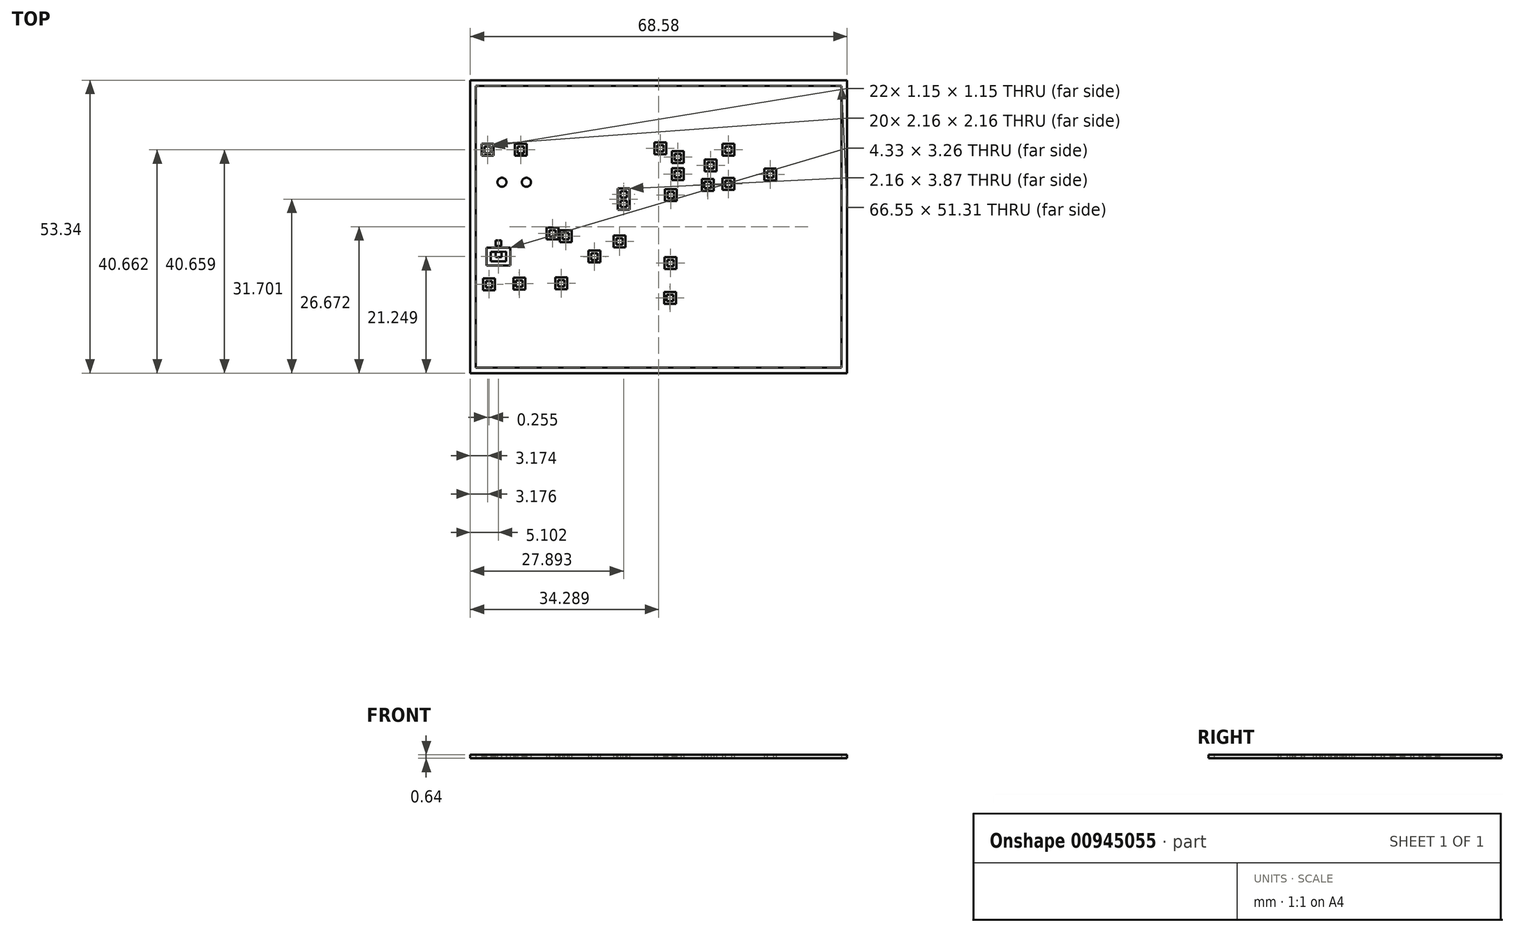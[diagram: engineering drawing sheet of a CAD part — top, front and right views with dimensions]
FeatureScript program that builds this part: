
annotation { "Feature Type Name" : "Feature", "Feature Type Description" : "" }
export const myFeature = defineFeature(function(context is Context, id is Id, definition is map)
    precondition{}
    {
        {
            var Q0;
            Q0=qCreatedBy(makeId("Top.planeOp"),FACE);
            var sketch = newSketch(context, id + "F0", { "sketchPlane" : qUnion([Q0])});
            skLineSegment(sketch, "E0.bottom", {"start": v(-43.28, 27.91) * mm, "end": v(25.3, 27.91) * mm});
            skLineSegment(sketch, "E0.top", {"start": v(-43.28, -25.43) * mm, "end": v(25.3, -25.43) * mm});
            skLineSegment(sketch, "E0.left", {"start": v(-43.28, 27.91) * mm, "end": v(-43.28, -25.43) * mm});
            skCircle(sketch, "E1", {"center": v(-37.53, 9.34) * mm, "radius": 0.82 * mm});
            skCircle(sketch, "E2", {"center": v(-37.53, 9.34) * mm, "radius": 1.33 * mm});
            skCircle(sketch, "E3", {"center": v(-33.07, 9.34) * mm, "radius": 0.83 * mm});
            skCircle(sketch, "E4", {"center": v(-33.07, 9.34) * mm, "radius": 1.33 * mm});
            skLineSegment(sketch, "E5.top", {"start": v(-39.58, -5.05) * mm, "end": v(-36.77, -5.05) * mm});
            skLineSegment(sketch, "E5.left", {"start": v(-39.58, -3.31) * mm, "end": v(-39.58, -5.05) * mm});
            skLineSegment(sketch, "E5.right", {"start": v(-36.77, -3.3) * mm, "end": v(-36.77, -5.05) * mm});
            skLineSegment(sketch, "E6.bottom", {"start": v(-38.67, -3.31) * mm, "end": v(-37.61, -3.31) * mm});
            skLineSegment(sketch, "E6.top", {"start": v(-38.67, -4.3) * mm, "end": v(-37.61, -4.3) * mm});
            skLineSegment(sketch, "E6.left", {"start": v(-38.67, -3.31) * mm, "end": v(-38.67, -4.3) * mm});
            skLineSegment(sketch, "E6.right", {"start": v(-37.61, -3.31) * mm, "end": v(-37.61, -4.3) * mm});
            skLineSegment(sketch, "E7", {"start": v(-39.58, -3.31) * mm, "end": v(-38.67, -3.31) * mm});
            skLineSegment(sketch, "E8", {"start": v(-36.77, -3.3) * mm, "end": v(-37.61, -3.31) * mm});
            skLineSegment(sketch, "E9", {"start": v(29.71, 21.65) * mm, "end": v(29.71, 63.81) * mm});
            skLineSegment(sketch, "E10.bottom", {"start": v(-38.67, -2.3) * mm, "end": v(-37.65, -2.3) * mm});
            skLineSegment(sketch, "E10.top", {"start": v(-38.67, -1.27) * mm, "end": v(-37.65, -1.27) * mm});
            skLineSegment(sketch, "E10.left", {"start": v(-38.67, -2.3) * mm, "end": v(-38.67, -1.27) * mm});
            skLineSegment(sketch, "E10.right", {"start": v(-37.65, -2.3) * mm, "end": v(-37.65, -1.27) * mm});
            skLineSegment(sketch, "E11.bottom", {"start": v(-40.42, -9.8) * mm, "end": v(-39.28, -9.8) * mm});
            skLineSegment(sketch, "E11.top", {"start": v(-40.42, -8.65) * mm, "end": v(-39.28, -8.65) * mm});
            skLineSegment(sketch, "E11.left", {"start": v(-40.42, -9.8) * mm, "end": v(-40.42, -8.65) * mm});
            skLineSegment(sketch, "E11.right", {"start": v(-39.28, -9.8) * mm, "end": v(-39.28, -8.65) * mm});
            skLineSegment(sketch, "E12.bottom", {"start": v(-40.93, -8.14) * mm, "end": v(-38.77, -8.14) * mm});
            skLineSegment(sketch, "E12.top", {"start": v(-40.93, -10.3) * mm, "end": v(-38.77, -10.3) * mm});
            skLineSegment(sketch, "E12.left", {"start": v(-40.93, -8.14) * mm, "end": v(-40.93, -10.3) * mm});
            skLineSegment(sketch, "E12.right", {"start": v(-38.77, -8.14) * mm, "end": v(-38.77, -10.3) * mm});
            skLineSegment(sketch, "E13.bottom", {"start": v(10.75, 10.18) * mm, "end": v(11.9, 10.18) * mm});
            skLineSegment(sketch, "E13.top", {"start": v(10.75, 11.32) * mm, "end": v(11.9, 11.32) * mm});
            skLineSegment(sketch, "E13.left", {"start": v(10.75, 10.18) * mm, "end": v(10.75, 11.32) * mm});
            skLineSegment(sketch, "E13.right", {"start": v(11.9, 10.18) * mm, "end": v(11.9, 11.32) * mm});
            skLineSegment(sketch, "E14.bottom", {"start": v(10.25, 11.83) * mm, "end": v(12.4, 11.83) * mm});
            skLineSegment(sketch, "E14.top", {"start": v(10.25, 9.67) * mm, "end": v(12.4, 9.67) * mm});
            skLineSegment(sketch, "E14.left", {"start": v(10.25, 11.83) * mm, "end": v(10.25, 9.67) * mm});
            skLineSegment(sketch, "E14.right", {"start": v(12.4, 11.83) * mm, "end": v(12.4, 9.67) * mm});
            skLineSegment(sketch, "E15.bottom", {"start": v(3.1, 8.44) * mm, "end": v(4.24, 8.44) * mm});
            skLineSegment(sketch, "E15.top", {"start": v(3.1, 9.58) * mm, "end": v(4.24, 9.58) * mm});
            skLineSegment(sketch, "E15.left", {"start": v(3.1, 8.44) * mm, "end": v(3.1, 9.58) * mm});
            skLineSegment(sketch, "E15.right", {"start": v(4.24, 8.44) * mm, "end": v(4.24, 9.58) * mm});
            skLineSegment(sketch, "E16.bottom", {"start": v(2.59, 10.1) * mm, "end": v(4.75, 10.1) * mm});
            skLineSegment(sketch, "E16.top", {"start": v(2.59, 7.93) * mm, "end": v(4.75, 7.93) * mm});
            skLineSegment(sketch, "E16.left", {"start": v(2.59, 10.1) * mm, "end": v(2.59, 7.93) * mm});
            skLineSegment(sketch, "E16.right", {"start": v(4.75, 10.1) * mm, "end": v(4.75, 7.93) * mm});
            skLineSegment(sketch, "E17.bottom", {"start": v(-0.67, 8.27) * mm, "end": v(0.48, 8.27) * mm});
            skLineSegment(sketch, "E17.top", {"start": v(-0.67, 9.41) * mm, "end": v(0.48, 9.41) * mm});
            skLineSegment(sketch, "E17.left", {"start": v(-0.67, 8.27) * mm, "end": v(-0.67, 9.41) * mm});
            skLineSegment(sketch, "E17.right", {"start": v(0.48, 8.27) * mm, "end": v(0.48, 9.41) * mm});
            skLineSegment(sketch, "E18.bottom", {"start": v(-1.17, 9.92) * mm, "end": v(0.98, 9.92) * mm});
            skLineSegment(sketch, "E18.top", {"start": v(-1.17, 7.76) * mm, "end": v(0.98, 7.76) * mm});
            skLineSegment(sketch, "E18.left", {"start": v(-1.17, 9.92) * mm, "end": v(-1.17, 7.76) * mm});
            skLineSegment(sketch, "E18.right", {"start": v(0.98, 9.92) * mm, "end": v(0.98, 7.76) * mm});
            skLineSegment(sketch, "E19.bottom", {"start": v(-0.1, 11.86) * mm, "end": v(1.05, 11.86) * mm});
            skLineSegment(sketch, "E19.top", {"start": v(-0.1, 13) * mm, "end": v(1.05, 13) * mm});
            skLineSegment(sketch, "E19.left", {"start": v(-0.1, 11.86) * mm, "end": v(-0.1, 13) * mm});
            skLineSegment(sketch, "E19.right", {"start": v(1.05, 11.86) * mm, "end": v(1.05, 13) * mm});
            skLineSegment(sketch, "E20.bottom", {"start": v(-0.6, 13.51) * mm, "end": v(1.56, 13.51) * mm});
            skLineSegment(sketch, "E20.top", {"start": v(-0.6, 11.35) * mm, "end": v(1.56, 11.35) * mm});
            skLineSegment(sketch, "E20.left", {"start": v(-0.6, 13.51) * mm, "end": v(-0.6, 11.35) * mm});
            skLineSegment(sketch, "E20.right", {"start": v(1.56, 13.51) * mm, "end": v(1.56, 11.35) * mm});
            skLineSegment(sketch, "E21.bottom", {"start": v(3.11, 14.7) * mm, "end": v(4.26, 14.7) * mm});
            skLineSegment(sketch, "E21.top", {"start": v(3.11, 15.85) * mm, "end": v(4.26, 15.85) * mm});
            skLineSegment(sketch, "E21.left", {"start": v(3.11, 14.7) * mm, "end": v(3.11, 15.85) * mm});
            skLineSegment(sketch, "E21.right", {"start": v(4.26, 14.7) * mm, "end": v(4.26, 15.85) * mm});
            skLineSegment(sketch, "E22.bottom", {"start": v(2.61, 16.36) * mm, "end": v(4.77, 16.36) * mm});
            skLineSegment(sketch, "E22.top", {"start": v(2.61, 14.2) * mm, "end": v(4.77, 14.2) * mm});
            skLineSegment(sketch, "E22.left", {"start": v(2.61, 16.36) * mm, "end": v(2.61, 14.2) * mm});
            skLineSegment(sketch, "E22.right", {"start": v(4.77, 16.36) * mm, "end": v(4.77, 14.2) * mm});
            skLineSegment(sketch, "E23.bottom", {"start": v(-9.3, 14.91) * mm, "end": v(-8.15, 14.91) * mm});
            skLineSegment(sketch, "E23.top", {"start": v(-9.3, 16.06) * mm, "end": v(-8.15, 16.06) * mm});
            skLineSegment(sketch, "E23.left", {"start": v(-9.3, 14.91) * mm, "end": v(-9.3, 16.06) * mm});
            skLineSegment(sketch, "E23.right", {"start": v(-8.15, 14.91) * mm, "end": v(-8.15, 16.06) * mm});
            skLineSegment(sketch, "E24.bottom", {"start": v(-9.8, 16.57) * mm, "end": v(-7.64, 16.57) * mm});
            skLineSegment(sketch, "E24.top", {"start": v(-9.8, 14.41) * mm, "end": v(-7.64, 14.41) * mm});
            skLineSegment(sketch, "E24.left", {"start": v(-9.8, 16.57) * mm, "end": v(-9.8, 14.41) * mm});
            skLineSegment(sketch, "E24.right", {"start": v(-7.64, 16.57) * mm, "end": v(-7.64, 14.41) * mm});
            skLineSegment(sketch, "E25.bottom", {"start": v(-6.09, 13.37) * mm, "end": v(-4.94, 13.37) * mm});
            skLineSegment(sketch, "E25.top", {"start": v(-6.09, 14.52) * mm, "end": v(-4.94, 14.52) * mm});
            skLineSegment(sketch, "E25.left", {"start": v(-6.09, 13.37) * mm, "end": v(-6.09, 14.52) * mm});
            skLineSegment(sketch, "E25.right", {"start": v(-4.94, 13.37) * mm, "end": v(-4.94, 14.52) * mm});
            skLineSegment(sketch, "E26.bottom", {"start": v(-6.59, 15.03) * mm, "end": v(-4.43, 15.03) * mm});
            skLineSegment(sketch, "E26.top", {"start": v(-6.59, 12.87) * mm, "end": v(-4.43, 12.87) * mm});
            skLineSegment(sketch, "E26.left", {"start": v(-6.59, 15.03) * mm, "end": v(-6.59, 12.87) * mm});
            skLineSegment(sketch, "E26.right", {"start": v(-4.43, 15.03) * mm, "end": v(-4.43, 12.87) * mm});
            skLineSegment(sketch, "E27.bottom", {"start": v(-6.1, 10.25) * mm, "end": v(-4.95, 10.25) * mm});
            skLineSegment(sketch, "E27.top", {"start": v(-6.1, 11.4) * mm, "end": v(-4.95, 11.4) * mm});
            skLineSegment(sketch, "E27.left", {"start": v(-6.1, 10.25) * mm, "end": v(-6.1, 11.4) * mm});
            skLineSegment(sketch, "E27.right", {"start": v(-4.95, 10.25) * mm, "end": v(-4.95, 11.4) * mm});
            skLineSegment(sketch, "E28.bottom", {"start": v(-6.6, 11.9) * mm, "end": v(-4.44, 11.9) * mm});
            skLineSegment(sketch, "E28.top", {"start": v(-6.6, 9.75) * mm, "end": v(-4.44, 9.75) * mm});
            skLineSegment(sketch, "E28.left", {"start": v(-6.6, 11.9) * mm, "end": v(-6.6, 9.75) * mm});
            skLineSegment(sketch, "E28.right", {"start": v(-4.44, 11.9) * mm, "end": v(-4.44, 9.75) * mm});
            skLineSegment(sketch, "E29.bottom", {"start": v(-7.39, 6.45) * mm, "end": v(-6.24, 6.45) * mm});
            skLineSegment(sketch, "E29.top", {"start": v(-7.39, 7.6) * mm, "end": v(-6.24, 7.6) * mm});
            skLineSegment(sketch, "E29.left", {"start": v(-7.39, 6.45) * mm, "end": v(-7.39, 7.6) * mm});
            skLineSegment(sketch, "E29.right", {"start": v(-6.24, 6.45) * mm, "end": v(-6.24, 7.6) * mm});
            skLineSegment(sketch, "E30.bottom", {"start": v(-7.9, 8.1) * mm, "end": v(-5.73, 8.1) * mm});
            skLineSegment(sketch, "E30.top", {"start": v(-7.9, 5.95) * mm, "end": v(-5.73, 5.95) * mm});
            skLineSegment(sketch, "E30.left", {"start": v(-7.9, 8.1) * mm, "end": v(-7.9, 5.95) * mm});
            skLineSegment(sketch, "E30.right", {"start": v(-5.73, 8.1) * mm, "end": v(-5.73, 5.95) * mm});
            skLineSegment(sketch, "E31.bottom", {"start": v(-7.43, -5.92) * mm, "end": v(-6.28, -5.92) * mm});
            skLineSegment(sketch, "E31.top", {"start": v(-7.43, -4.78) * mm, "end": v(-6.28, -4.78) * mm});
            skLineSegment(sketch, "E31.left", {"start": v(-7.43, -5.92) * mm, "end": v(-7.43, -4.78) * mm});
            skLineSegment(sketch, "E31.right", {"start": v(-6.28, -5.92) * mm, "end": v(-6.28, -4.78) * mm});
            skLineSegment(sketch, "E32.bottom", {"start": v(-7.93, -4.27) * mm, "end": v(-5.77, -4.27) * mm});
            skLineSegment(sketch, "E32.top", {"start": v(-7.93, -6.43) * mm, "end": v(-5.77, -6.43) * mm});
            skLineSegment(sketch, "E32.left", {"start": v(-7.93, -4.27) * mm, "end": v(-7.93, -6.43) * mm});
            skLineSegment(sketch, "E32.right", {"start": v(-5.77, -4.27) * mm, "end": v(-5.77, -6.43) * mm});
            skLineSegment(sketch, "E33.bottom", {"start": v(-7.53, -12.3) * mm, "end": v(-6.38, -12.3) * mm});
            skLineSegment(sketch, "E33.top", {"start": v(-7.53, -11.14) * mm, "end": v(-6.38, -11.14) * mm});
            skLineSegment(sketch, "E33.left", {"start": v(-7.53, -12.3) * mm, "end": v(-7.53, -11.14) * mm});
            skLineSegment(sketch, "E33.right", {"start": v(-6.38, -12.3) * mm, "end": v(-6.38, -11.14) * mm});
            skLineSegment(sketch, "E34.bottom", {"start": v(-8.03, -10.63) * mm, "end": v(-5.87, -10.63) * mm});
            skLineSegment(sketch, "E34.top", {"start": v(-8.03, -12.8) * mm, "end": v(-5.87, -12.8) * mm});
            skLineSegment(sketch, "E34.left", {"start": v(-8.03, -10.63) * mm, "end": v(-8.03, -12.8) * mm});
            skLineSegment(sketch, "E34.right", {"start": v(-5.87, -10.63) * mm, "end": v(-5.87, -12.8) * mm});
            skLineSegment(sketch, "E35.bottom", {"start": v(-15.96, 6.55) * mm, "end": v(-14.82, 6.55) * mm});
            skLineSegment(sketch, "E35.top", {"start": v(-15.96, 7.7) * mm, "end": v(-14.82, 7.7) * mm});
            skLineSegment(sketch, "E35.left", {"start": v(-15.96, 6.55) * mm, "end": v(-15.96, 7.7) * mm});
            skLineSegment(sketch, "E35.right", {"start": v(-14.82, 6.55) * mm, "end": v(-14.82, 7.7) * mm});
            skLineSegment(sketch, "E36.bottom", {"start": v(-16.47, 8.2) * mm, "end": v(-14.3, 8.2) * mm});
            skLineSegment(sketch, "E36.top", {"start": v(-16.47, 6.05) * mm, "end": v(-14.3, 6.05) * mm});
            skLineSegment(sketch, "E36.left", {"start": v(-16.47, 8.2) * mm, "end": v(-16.47, 6.05) * mm});
            skLineSegment(sketch, "E36.right", {"start": v(-14.3, 8.2) * mm, "end": v(-14.3, 6.05) * mm});
            skLineSegment(sketch, "E37.bottom", {"start": v(-15.96, 4.84) * mm, "end": v(-14.82, 4.84) * mm});
            skLineSegment(sketch, "E37.top", {"start": v(-15.96, 5.99) * mm, "end": v(-14.82, 5.99) * mm});
            skLineSegment(sketch, "E37.left", {"start": v(-15.96, 4.84) * mm, "end": v(-15.96, 5.99) * mm});
            skLineSegment(sketch, "E37.right", {"start": v(-14.82, 4.84) * mm, "end": v(-14.82, 5.99) * mm});
            skLineSegment(sketch, "E38.bottom", {"start": v(-16.47, 6.5) * mm, "end": v(-14.3, 6.5) * mm});
            skLineSegment(sketch, "E38.top", {"start": v(-16.47, 4.34) * mm, "end": v(-14.3, 4.34) * mm});
            skLineSegment(sketch, "E38.left", {"start": v(-16.47, 6.5) * mm, "end": v(-16.47, 4.34) * mm});
            skLineSegment(sketch, "E38.right", {"start": v(-14.3, 6.5) * mm, "end": v(-14.3, 4.34) * mm});
            skLineSegment(sketch, "E39.bottom", {"start": v(-34.67, 14.66) * mm, "end": v(-33.52, 14.66) * mm});
            skLineSegment(sketch, "E39.top", {"start": v(-34.67, 15.8) * mm, "end": v(-33.52, 15.8) * mm});
            skLineSegment(sketch, "E39.left", {"start": v(-34.67, 14.66) * mm, "end": v(-34.67, 15.8) * mm});
            skLineSegment(sketch, "E39.right", {"start": v(-33.52, 14.66) * mm, "end": v(-33.52, 15.8) * mm});
            skLineSegment(sketch, "E40.bottom", {"start": v(-35.17, 16.31) * mm, "end": v(-33.01, 16.31) * mm});
            skLineSegment(sketch, "E40.top", {"start": v(-35.17, 14.15) * mm, "end": v(-33.01, 14.15) * mm});
            skLineSegment(sketch, "E40.left", {"start": v(-35.17, 16.31) * mm, "end": v(-35.17, 14.15) * mm});
            skLineSegment(sketch, "E40.right", {"start": v(-33.01, 16.31) * mm, "end": v(-33.01, 14.15) * mm});
            skLineSegment(sketch, "E41.bottom", {"start": v(-40.68, 14.66) * mm, "end": v(-39.53, 14.66) * mm});
            skLineSegment(sketch, "E41.top", {"start": v(-40.68, 15.8) * mm, "end": v(-39.53, 15.8) * mm});
            skLineSegment(sketch, "E41.left", {"start": v(-40.68, 14.66) * mm, "end": v(-40.68, 15.8) * mm});
            skLineSegment(sketch, "E41.right", {"start": v(-39.53, 14.66) * mm, "end": v(-39.53, 15.8) * mm});
            skLineSegment(sketch, "E42.bottom", {"start": v(-41.18, 16.31) * mm, "end": v(-39.02, 16.31) * mm});
            skLineSegment(sketch, "E42.top", {"start": v(-41.18, 14.15) * mm, "end": v(-39.02, 14.15) * mm});
            skLineSegment(sketch, "E42.left", {"start": v(-41.18, 16.31) * mm, "end": v(-41.18, 14.15) * mm});
            skLineSegment(sketch, "E42.right", {"start": v(-39.02, 16.31) * mm, "end": v(-39.02, 14.15) * mm});
            skLineSegment(sketch, "E43.bottom", {"start": v(-16.68, -2.03) * mm, "end": v(-15.54, -2.03) * mm});
            skLineSegment(sketch, "E43.top", {"start": v(-16.68, -0.88) * mm, "end": v(-15.54, -0.88) * mm});
            skLineSegment(sketch, "E43.left", {"start": v(-16.68, -2.03) * mm, "end": v(-16.68, -0.88) * mm});
            skLineSegment(sketch, "E43.right", {"start": v(-15.54, -2.03) * mm, "end": v(-15.54, -0.88) * mm});
            skLineSegment(sketch, "E44.bottom", {"start": v(-17.19, -0.38) * mm, "end": v(-15.03, -0.38) * mm});
            skLineSegment(sketch, "E44.top", {"start": v(-17.19, -2.54) * mm, "end": v(-15.03, -2.54) * mm});
            skLineSegment(sketch, "E44.left", {"start": v(-17.19, -0.38) * mm, "end": v(-17.19, -2.54) * mm});
            skLineSegment(sketch, "E44.right", {"start": v(-15.03, -0.38) * mm, "end": v(-15.03, -2.54) * mm});
            skLineSegment(sketch, "E45.bottom", {"start": v(-21.25, -4.78) * mm, "end": v(-20.1, -4.78) * mm});
            skLineSegment(sketch, "E45.top", {"start": v(-21.25, -3.63) * mm, "end": v(-20.1, -3.63) * mm});
            skLineSegment(sketch, "E45.left", {"start": v(-21.25, -4.78) * mm, "end": v(-21.25, -3.63) * mm});
            skLineSegment(sketch, "E45.right", {"start": v(-20.1, -4.78) * mm, "end": v(-20.1, -3.63) * mm});
            skLineSegment(sketch, "E46.bottom", {"start": v(-21.76, -3.12) * mm, "end": v(-19.6, -3.12) * mm});
            skLineSegment(sketch, "E46.top", {"start": v(-21.76, -5.28) * mm, "end": v(-19.6, -5.28) * mm});
            skLineSegment(sketch, "E46.left", {"start": v(-21.76, -3.12) * mm, "end": v(-21.76, -5.28) * mm});
            skLineSegment(sketch, "E46.right", {"start": v(-19.6, -3.12) * mm, "end": v(-19.6, -5.28) * mm});
            skLineSegment(sketch, "E47.bottom", {"start": v(-26.47, -1.04) * mm, "end": v(-25.32, -1.04) * mm});
            skLineSegment(sketch, "E47.top", {"start": v(-26.47, 0.1) * mm, "end": v(-25.32, 0.1) * mm});
            skLineSegment(sketch, "E47.left", {"start": v(-26.47, -1.04) * mm, "end": v(-26.47, 0.1) * mm});
            skLineSegment(sketch, "E47.right", {"start": v(-25.32, -1.04) * mm, "end": v(-25.32, 0.1) * mm});
            skLineSegment(sketch, "E48.bottom", {"start": v(-26.97, 0.62) * mm, "end": v(-24.81, 0.62) * mm});
            skLineSegment(sketch, "E48.top", {"start": v(-26.97, -1.54) * mm, "end": v(-24.81, -1.54) * mm});
            skLineSegment(sketch, "E48.left", {"start": v(-26.97, 0.62) * mm, "end": v(-26.97, -1.54) * mm});
            skLineSegment(sketch, "E48.right", {"start": v(-24.81, 0.62) * mm, "end": v(-24.81, -1.54) * mm});
            skLineSegment(sketch, "E49.bottom", {"start": v(-28.9, -0.55) * mm, "end": v(-27.75, -0.55) * mm});
            skLineSegment(sketch, "E49.top", {"start": v(-28.9, 0.6) * mm, "end": v(-27.75, 0.6) * mm});
            skLineSegment(sketch, "E49.left", {"start": v(-28.9, -0.55) * mm, "end": v(-28.9, 0.6) * mm});
            skLineSegment(sketch, "E49.right", {"start": v(-27.75, -0.55) * mm, "end": v(-27.75, 0.6) * mm});
            skLineSegment(sketch, "E50.bottom", {"start": v(-29.4, 1.1) * mm, "end": v(-27.24, 1.1) * mm});
            skLineSegment(sketch, "E50.top", {"start": v(-29.4, -1.05) * mm, "end": v(-27.24, -1.05) * mm});
            skLineSegment(sketch, "E50.left", {"start": v(-29.4, 1.1) * mm, "end": v(-29.4, -1.05) * mm});
            skLineSegment(sketch, "E50.right", {"start": v(-27.24, 1.1) * mm, "end": v(-27.24, -1.05) * mm});
            skLineSegment(sketch, "E51.bottom", {"start": v(-27.3, -9.64) * mm, "end": v(-26.14, -9.64) * mm});
            skLineSegment(sketch, "E51.top", {"start": v(-27.3, -8.5) * mm, "end": v(-26.14, -8.5) * mm});
            skLineSegment(sketch, "E51.left", {"start": v(-27.3, -9.64) * mm, "end": v(-27.3, -8.5) * mm});
            skLineSegment(sketch, "E51.right", {"start": v(-26.14, -9.64) * mm, "end": v(-26.14, -8.5) * mm});
            skLineSegment(sketch, "E52.bottom", {"start": v(-27.8, -7.99) * mm, "end": v(-25.64, -7.99) * mm});
            skLineSegment(sketch, "E52.top", {"start": v(-27.8, -10.15) * mm, "end": v(-25.64, -10.15) * mm});
            skLineSegment(sketch, "E52.left", {"start": v(-27.8, -7.99) * mm, "end": v(-27.8, -10.15) * mm});
            skLineSegment(sketch, "E52.right", {"start": v(-25.64, -7.99) * mm, "end": v(-25.64, -10.15) * mm});
            skLineSegment(sketch, "E53.bottom", {"start": v(-34.96, -9.7) * mm, "end": v(-33.81, -9.7) * mm});
            skLineSegment(sketch, "E53.top", {"start": v(-34.96, -8.55) * mm, "end": v(-33.81, -8.55) * mm});
            skLineSegment(sketch, "E53.left", {"start": v(-34.96, -9.7) * mm, "end": v(-34.96, -8.55) * mm});
            skLineSegment(sketch, "E53.right", {"start": v(-33.81, -9.7) * mm, "end": v(-33.81, -8.55) * mm});
            skLineSegment(sketch, "E54.bottom", {"start": v(-35.46, -8.05) * mm, "end": v(-33.3, -8.05) * mm});
            skLineSegment(sketch, "E54.top", {"start": v(-35.46, -10.2) * mm, "end": v(-33.3, -10.2) * mm});
            skLineSegment(sketch, "E54.left", {"start": v(-35.46, -8.05) * mm, "end": v(-35.46, -10.2) * mm});
            skLineSegment(sketch, "E54.right", {"start": v(-33.3, -8.05) * mm, "end": v(-33.3, -10.2) * mm});
            skLineSegment(sketch, "E55.bottom", {"start": v(-39.58, -3.31) * mm, "end": v(-36.84, -3.31) * mm});
            skLineSegment(sketch, "E56.left", {"start": v(40.01, 22.16) * mm, "end": v(40.01, 20) * mm});
            skLineSegment(sketch, "E57", {"start": v(25.3, -25.43) * mm, "end": v(25.3, 27.91) * mm});
            skLineSegment(sketch, "E58.bottom", {"start": v(-42.27, 26.9) * mm, "end": v(24.28, 26.9) * mm});
            skLineSegment(sketch, "E58.top", {"start": v(-42.27, -24.41) * mm, "end": v(24.28, -24.41) * mm});
            skLineSegment(sketch, "E58.left", {"start": v(-42.27, 26.9) * mm, "end": v(-42.27, -24.41) * mm});
            skLineSegment(sketch, "E58.right", {"start": v(24.28, 26.9) * mm, "end": v(24.28, -24.41) * mm});
            skLineSegment(sketch, "E59.bottom", {"start": v(-40.34, -2.55) * mm, "end": v(-36.01, -2.55) * mm});
            skLineSegment(sketch, "E59.top", {"start": v(-40.34, -5.81) * mm, "end": v(-36.01, -5.81) * mm});
            skLineSegment(sketch, "E59.left", {"start": v(-40.34, -2.55) * mm, "end": v(-40.34, -5.81) * mm});
            skLineSegment(sketch, "E59.right", {"start": v(-36.01, -2.55) * mm, "end": v(-36.01, -5.81) * mm});
            skSolve(sketch);
        }
        {
            var Q0;
            Q0=makeQuery(id+"F0.imprint","IMPRINT",FACE,{"disambiguationData":[TD([[makeQuery(id+"F0.imprint","IMPRINT",EDGE,{"derivedFrom":sQuery(id+"F0.wireOp",EDGE,"E2")}),-1.0]])]});
            var Q1;
            Q1=makeQuery(id+"F0.imprint","IMPRINT",FACE,{"disambiguationData":[TD([[makeQuery(id+"F0.imprint","IMPRINT",EDGE,{"derivedFrom":sQuery(id+"F0.wireOp",EDGE,"E41.bottom")}),1.0]])]});
            var Q2;
            Q2=makeQuery(id+"F0.imprint","IMPRINT",FACE,{"disambiguationData":[TD([[makeQuery(id+"F0.imprint","IMPRINT",EDGE,{"derivedFrom":sQuery(id+"F0.wireOp",EDGE,"E39.bottom")}),1.0]])]});
            var Q3;
            Q3=makeQuery(id+"F0.imprint","IMPRINT",FACE,{"disambiguationData":[TD([[makeQuery(id+"F0.imprint","IMPRINT",EDGE,{"derivedFrom":sQuery(id+"F0.wireOp",EDGE,"E1")}),-1.0]])]});
            var Q4;
            Q4=makeQuery(id+"F0.imprint","IMPRINT",FACE,{"disambiguationData":[TD([[makeQuery(id+"F0.imprint","IMPRINT",EDGE,{"derivedFrom":sQuery(id+"F0.wireOp",EDGE,"E3")}),-1.0]])]});
            var Q5;
            Q5=makeQuery(id+"F0.imprint","IMPRINT",FACE,{"disambiguationData":[TD([[makeQuery(id+"F0.imprint","IMPRINT",EDGE,{"derivedFrom":sQuery(id+"F0.wireOp",EDGE,"E5.top")}),1.0]])]});
            var Q6;
            Q6=makeQuery(id+"F0.imprint","IMPRINT",FACE,{"disambiguationData":[TD([[makeQuery(id+"F0.imprint","IMPRINT",EDGE,{"derivedFrom":sQuery(id+"F0.wireOp",EDGE,"E11.bottom")}),1.0]])]});
            var Q7;
            Q7=makeQuery(id+"F0.imprint","IMPRINT",FACE,{"disambiguationData":[TD([[makeQuery(id+"F0.imprint","IMPRINT",EDGE,{"derivedFrom":sQuery(id+"F0.wireOp",EDGE,"E53.bottom")}),1.0]])]});
            var Q8;
            Q8=makeQuery(id+"F0.imprint","IMPRINT",FACE,{"disambiguationData":[TD([[makeQuery(id+"F0.imprint","IMPRINT",EDGE,{"derivedFrom":sQuery(id+"F0.wireOp",EDGE,"E51.bottom")}),1.0]])]});
            var Q9;
            Q9=makeQuery(id+"F0.imprint","IMPRINT",FACE,{"disambiguationData":[TD([[makeQuery(id+"F0.imprint","IMPRINT",EDGE,{"derivedFrom":sQuery(id+"F0.wireOp",EDGE,"E49.bottom")}),1.0]])]});
            var Q10;
            Q10=makeQuery(id+"F0.imprint","IMPRINT",FACE,{"disambiguationData":[TD([[makeQuery(id+"F0.imprint","IMPRINT",EDGE,{"derivedFrom":sQuery(id+"F0.wireOp",EDGE,"E47.bottom")}),1.0]])]});
            var Q11;
            Q11=makeQuery(id+"F0.imprint","IMPRINT",FACE,{"disambiguationData":[TD([[makeQuery(id+"F0.imprint","IMPRINT",EDGE,{"derivedFrom":sQuery(id+"F0.wireOp",EDGE,"E45.bottom")}),1.0]])]});
            var Q12;
            Q12=makeQuery(id+"F0.imprint","IMPRINT",FACE,{"disambiguationData":[TD([[makeQuery(id+"F0.imprint","IMPRINT",EDGE,{"derivedFrom":sQuery(id+"F0.wireOp",EDGE,"E43.bottom")}),1.0]])]});
            var Q13;
            Q13=makeQuery(id+"F0.imprint","IMPRINT",FACE,{"disambiguationData":[TD([[makeQuery(id+"F0.imprint","IMPRINT",EDGE,{"derivedFrom":sQuery(id+"F0.wireOp",EDGE,"E37.bottom")}),1.0]])]});
            var Q14;
            Q14=makeQuery(id+"F0.imprint","IMPRINT",FACE,{"disambiguationData":[TD([[makeQuery(id+"F0.imprint","IMPRINT",EDGE,{"derivedFrom":sQuery(id+"F0.wireOp",EDGE,"E27.bottom")}),1.0]])]});
            var Q15;
            Q15=makeQuery(id+"F0.imprint","IMPRINT",FACE,{"disambiguationData":[TD([[makeQuery(id+"F0.imprint","IMPRINT",EDGE,{"derivedFrom":sQuery(id+"F0.wireOp",EDGE,"E29.bottom")}),1.0]])]});
            var Q16;
            Q16=makeQuery(id+"F0.imprint","IMPRINT",FACE,{"disambiguationData":[TD([[makeQuery(id+"F0.imprint","IMPRINT",EDGE,{"derivedFrom":sQuery(id+"F0.wireOp",EDGE,"E33.bottom")}),1.0]])]});
            var Q17;
            Q17=makeQuery(id+"F0.imprint","IMPRINT",FACE,{"disambiguationData":[TD([[makeQuery(id+"F0.imprint","IMPRINT",EDGE,{"derivedFrom":sQuery(id+"F0.wireOp",EDGE,"E31.bottom")}),1.0]])]});
            var Q18;
            Q18=makeQuery(id+"F0.imprint","IMPRINT",FACE,{"disambiguationData":[TD([[makeQuery(id+"F0.imprint","IMPRINT",EDGE,{"derivedFrom":sQuery(id+"F0.wireOp",EDGE,"E23.bottom")}),1.0]])]});
            var Q19;
            Q19=makeQuery(id+"F0.imprint","IMPRINT",FACE,{"disambiguationData":[TD([[makeQuery(id+"F0.imprint","IMPRINT",EDGE,{"derivedFrom":sQuery(id+"F0.wireOp",EDGE,"E35.bottom")}),1.0]])]});
            var Q20;
            Q20=makeQuery(id+"F0.imprint","IMPRINT",FACE,{"disambiguationData":[TD([[makeQuery(id+"F0.imprint","IMPRINT",EDGE,{"derivedFrom":sQuery(id+"F0.wireOp",EDGE,"E25.bottom")}),1.0]])]});
            var Q21;
            Q21=makeQuery(id+"F0.imprint","IMPRINT",FACE,{"disambiguationData":[TD([[makeQuery(id+"F0.imprint","IMPRINT",EDGE,{"derivedFrom":sQuery(id+"F0.wireOp",EDGE,"E19.bottom")}),1.0]])]});
            var Q22;
            Q22=makeQuery(id+"F0.imprint","IMPRINT",FACE,{"disambiguationData":[TD([[makeQuery(id+"F0.imprint","IMPRINT",EDGE,{"derivedFrom":sQuery(id+"F0.wireOp",EDGE,"E21.bottom")}),1.0]])]});
            var Q23;
            Q23=makeQuery(id+"F0.imprint","IMPRINT",FACE,{"disambiguationData":[TD([[makeQuery(id+"F0.imprint","IMPRINT",EDGE,{"derivedFrom":sQuery(id+"F0.wireOp",EDGE,"E17.bottom")}),1.0]])]});
            var Q24;
            Q24=makeQuery(id+"F0.imprint","IMPRINT",FACE,{"disambiguationData":[TD([[makeQuery(id+"F0.imprint","IMPRINT",EDGE,{"derivedFrom":sQuery(id+"F0.wireOp",EDGE,"E15.bottom")}),1.0]])]});
            var Q25;
            Q25=makeQuery(id+"F0.imprint","IMPRINT",FACE,{"disambiguationData":[TD([[makeQuery(id+"F0.imprint","IMPRINT",EDGE,{"derivedFrom":sQuery(id+"F0.wireOp",EDGE,"E13.bottom")}),1.0]])]});
            extrude(context, id + "F1", {"entities" : qUnion([Q0, Q1, Q2, Q3, Q4, Q5, Q6, Q7, Q8, Q9, Q10, Q11, Q12, Q13, Q14, Q15, Q16, Q17, Q18, Q19, Q20, Q21, Q22, Q23, Q24, Q25]), "depth" : 0.64 * mm, "offsetDistance" : 25.4 * mm});
        }
        {
            var Q0;
            Q0 = qSketchRegion(id + "F0", true);
            var Q1;
            Q1=makeQuery(id+"F0.imprint","IMPRINT",FACE,{"disambiguationData":[TD([[makeQuery(id+"F0.imprint","IMPRINT",EDGE,{"derivedFrom":sQuery(id+"F0.wireOp",EDGE,"E39.bottom")}),-1.0]])]});
            var Q2;
            Q2=makeQuery(id+"F0.imprint","IMPRINT",FACE,{"disambiguationData":[TD([[makeQuery(id+"F0.imprint","IMPRINT",EDGE,{"derivedFrom":sQuery(id+"F0.wireOp",EDGE,"E41.bottom")}),-1.0]])]});
            var Q3;
            Q3=makeQuery(id+"F0.imprint","IMPRINT",FACE,{"disambiguationData":[TD([[makeQuery(id+"F0.imprint","IMPRINT",EDGE,{"derivedFrom":sQuery(id+"F0.wireOp",EDGE,"E5.top")}),-1.0]])]});
            var Q4;
            Q4=makeQuery(id+"F0.imprint","IMPRINT",FACE,{"disambiguationData":[TD([[makeQuery(id+"F0.imprint","IMPRINT",EDGE,{"derivedFrom":sQuery(id+"F0.wireOp",EDGE,"E49.bottom")}),-1.0]])]});
            var Q5;
            Q5=makeQuery(id+"F0.imprint","IMPRINT",FACE,{"disambiguationData":[TD([[makeQuery(id+"F0.imprint","IMPRINT",EDGE,{"derivedFrom":sQuery(id+"F0.wireOp",EDGE,"E47.bottom")}),-1.0]])]});
            var Q6;
            Q6=makeQuery(id+"F0.imprint","IMPRINT",FACE,{"disambiguationData":[TD([[makeQuery(id+"F0.imprint","IMPRINT",EDGE,{"derivedFrom":sQuery(id+"F0.wireOp",EDGE,"E45.bottom")}),-1.0]])]});
            var Q7;
            Q7=makeQuery(id+"F0.imprint","IMPRINT",FACE,{"disambiguationData":[TD([[makeQuery(id+"F0.imprint","IMPRINT",EDGE,{"derivedFrom":sQuery(id+"F0.wireOp",EDGE,"E43.bottom")}),-1.0]])]});
            var Q8;
            {var subQ0=sQuery(id+"F0.wireOp",EDGE,"E36.top");Q8=makeQuery(id+"F0.imprint","IMPRINT",FACE,{"disambiguationData":[TD([[makeQuery(id+"F0.imprint","IMPRINT",EDGE,{"derivedFrom":subQ0}),1.0]])]});}
            var Q9;
            {var subQ0=sQuery(id+"F0.wireOp",EDGE,"E36.top");Q9=makeQuery(id+"F0.imprint","IMPRINT",FACE,{"disambiguationData":[TD([[makeQuery(id+"F0.imprint","IMPRINT",EDGE,{"derivedFrom":subQ0}),-1.0]])]});}
            var Q10;
            Q10=makeQuery(id+"F0.imprint","IMPRINT",FACE,{"disambiguationData":[TD([[makeQuery(id+"F0.imprint","IMPRINT",EDGE,{"derivedFrom":sQuery(id+"F0.wireOp",EDGE,"E35.bottom")}),-1.0]])]});
            var Q11;
            Q11=makeQuery(id+"F0.imprint","IMPRINT",FACE,{"disambiguationData":[TD([[makeQuery(id+"F0.imprint","IMPRINT",EDGE,{"derivedFrom":sQuery(id+"F0.wireOp",EDGE,"E23.bottom")}),-1.0]])]});
            var Q12;
            Q12=makeQuery(id+"F0.imprint","IMPRINT",FACE,{"disambiguationData":[TD([[makeQuery(id+"F0.imprint","IMPRINT",EDGE,{"derivedFrom":sQuery(id+"F0.wireOp",EDGE,"E25.bottom")}),-1.0]])]});
            var Q13;
            Q13=makeQuery(id+"F0.imprint","IMPRINT",FACE,{"disambiguationData":[TD([[makeQuery(id+"F0.imprint","IMPRINT",EDGE,{"derivedFrom":sQuery(id+"F0.wireOp",EDGE,"E27.bottom")}),-1.0]])]});
            var Q14;
            Q14=makeQuery(id+"F0.imprint","IMPRINT",FACE,{"disambiguationData":[TD([[makeQuery(id+"F0.imprint","IMPRINT",EDGE,{"derivedFrom":sQuery(id+"F0.wireOp",EDGE,"E29.bottom")}),-1.0]])]});
            var Q15;
            Q15=makeQuery(id+"F0.imprint","IMPRINT",FACE,{"disambiguationData":[TD([[makeQuery(id+"F0.imprint","IMPRINT",EDGE,{"derivedFrom":sQuery(id+"F0.wireOp",EDGE,"E17.bottom")}),-1.0]])]});
            var Q16;
            Q16=makeQuery(id+"F0.imprint","IMPRINT",FACE,{"disambiguationData":[TD([[makeQuery(id+"F0.imprint","IMPRINT",EDGE,{"derivedFrom":sQuery(id+"F0.wireOp",EDGE,"E19.bottom")}),-1.0]])]});
            var Q17;
            Q17=makeQuery(id+"F0.imprint","IMPRINT",FACE,{"disambiguationData":[TD([[makeQuery(id+"F0.imprint","IMPRINT",EDGE,{"derivedFrom":sQuery(id+"F0.wireOp",EDGE,"E21.bottom")}),-1.0]])]});
            var Q18;
            Q18=makeQuery(id+"F0.imprint","IMPRINT",FACE,{"disambiguationData":[TD([[makeQuery(id+"F0.imprint","IMPRINT",EDGE,{"derivedFrom":sQuery(id+"F0.wireOp",EDGE,"E15.bottom")}),-1.0]])]});
            var Q19;
            Q19=makeQuery(id+"F0.imprint","IMPRINT",FACE,{"disambiguationData":[TD([[makeQuery(id+"F0.imprint","IMPRINT",EDGE,{"derivedFrom":sQuery(id+"F0.wireOp",EDGE,"E31.bottom")}),-1.0]])]});
            var Q20;
            Q20=makeQuery(id+"F0.imprint","IMPRINT",FACE,{"disambiguationData":[TD([[makeQuery(id+"F0.imprint","IMPRINT",EDGE,{"derivedFrom":sQuery(id+"F0.wireOp",EDGE,"E13.bottom")}),-1.0]])]});
            var Q21;
            Q21=makeQuery(id+"F0.imprint","IMPRINT",FACE,{"disambiguationData":[TD([[makeQuery(id+"F0.imprint","IMPRINT",EDGE,{"derivedFrom":sQuery(id+"F0.wireOp",EDGE,"E33.bottom")}),-1.0]])]});
            var Q22;
            Q22=makeQuery(id+"F0.imprint","IMPRINT",FACE,{"disambiguationData":[TD([[makeQuery(id+"F0.imprint","IMPRINT",EDGE,{"derivedFrom":sQuery(id+"F0.wireOp",EDGE,"E51.bottom")}),-1.0]])]});
            var Q23;
            Q23=makeQuery(id+"F0.imprint","IMPRINT",FACE,{"disambiguationData":[TD([[makeQuery(id+"F0.imprint","IMPRINT",EDGE,{"derivedFrom":sQuery(id+"F0.wireOp",EDGE,"E53.bottom")}),-1.0]])]});
            var Q24;
            Q24=makeQuery(id+"F0.imprint","IMPRINT",FACE,{"disambiguationData":[TD([[makeQuery(id+"F0.imprint","IMPRINT",EDGE,{"derivedFrom":sQuery(id+"F0.wireOp",EDGE,"E11.bottom")}),-1.0]])]});
            extrude(context, id + "F2", {"entities" : qUnion([Q0, Q1, Q2, Q3, Q4, Q5, Q6, Q7, Q8, Q9, Q10, Q11, Q12, Q13, Q14, Q15, Q16, Q17, Q18, Q19, Q20, Q21, Q22, Q23, Q24]), "depth" : 0.64 * mm, "offsetDistance" : 25.4 * mm});
        }
    });
